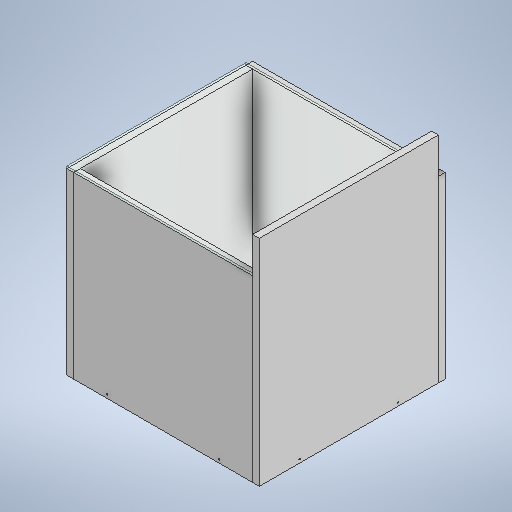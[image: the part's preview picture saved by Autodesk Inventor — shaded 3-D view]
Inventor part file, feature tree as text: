
AUTODESK INVENTOR PART (.ipt)
format: ipt  version: 2025.1 (Build 291241000, 241)  size: 359,936 bytes
history: native  units: mm
features: other x25, extrude x12, sketch x12, imported_body x1
ambient origin geometry x8: Origin, YZ Plane, XZ Plane, XY Plane, X Axis, Y Axis, Z Axis, Center Point
bodies: Body1 (feature_tree), Body2 (feature_tree), Body3 (feature_tree), Body4 (feature_tree), Body5 (feature_tree), Body6 (feature_tree), Body7 (feature_tree)
feature tree (50):
  other  "Sólido1"
  extrude  "Extrusão1"  Depth=400.0mm
  extrude  "Extrusão2"  Depth=200.0mm
  extrude  "Extrusão4"  Depth=400.0mm
  extrude  "Extrusão9"  Depth=15.0mm TaperAngle=0.0deg
  extrude  "Extrusão10"  Depth=400.0mm
  extrude  "Extrusão11"  Depth=15.0mm TaperAngle=0.0deg
  other  "Plano de trabalho1"
  extrude  "Extrusão12"  Depth=5.0mm
  extrude  "Extrusão13"  Depth=75.0mm
  extrude  "Extrusão14"  Depth=75.0mm
  extrude  "Extrusão15"  Depth=40.0mm
  extrude  "Extrusão16"  Depth=15.0mm TaperAngle=0.0deg
  extrude  "Extrusão17"  Depth=75.0mm
  sketch  "Esboço1"  dims[d0=400.0mm d1=400.0mm]
  sketch  "Esboço2"  dims[d2=200.0mm d3=200.0mm]
  other  "Contorno projetado1"
  other  "Sólido2"
  sketch  "Esboço4"  dims[d4=15.0mm d5=0.0mm d7=400.0mm]
  other  "Contorno projetado5"
  other  "Contorno projetado6"
  other  "Sólido4"
  imported_body  "base"
  sketch  "Esboço10"  dims[d8=15.0mm d9=0.0mm d12=15.0mm d13=0.0mm]
  other  "Contorno projetado17"
  other  "Contorno projetado18"
  other  "Sólido9"
  sketch  "Esboço11"  dims[d29=15.0mm d30=0.0mm d31=400.0mm]
  sketch  "Esboço12"  dims[d32=80.0mm d33=15.0mm d34=0.0mm]
  other  "Contorno projetado19"
  other  "vidro"
  sketch  "Esboço15"  dims[d35=5.0mm d36=0.0mm d37=3.0mm]
  sketch  "Esboço16"  dims[d38=75.0mm d39=3.0mm]
  other  "Contorno projetado23"
  other  "Contorno projetado24"
  other  "Contorno projetado25"
  other  "Sólido11"
  sketch  "Esboço17"  dims[d40=75.0mm d41=7.5mm]
  other  "Contorno projetado26"
  other  "Contorno projetado27"
  other  "Contorno projetado28"
  other  "Contorno projetado29"
  sketch  "Esboço18"  dims[d42=50000.0mm d43=0.0mm d44=40.0mm]
  other  "Contorno projetado30"
  other  "Contorno projetado31"
  other  "Contorno projetado32"
  other  "Sólido12"
  other  "Contorno projetado33"
  sketch  "Esboço19"  dims[d45=15.0mm d46=0.0mm d47=15.0mm d48=0.0mm]
  sketch  "Esboço20"  dims[d49=15.0mm d50=0.0mm d51=4.0mm d52=75.0mm d53=7.5mm d54=4.0mm d55=75.0mm d56=5000.0mm d57=0.0mm d58=4.0mm d59=75.0mm d60=20.0mm d61=4.0mm d62=75.0mm d63=20.0mm d64=5000.0mm d65=0.0mm d18=0.5mm d19=0.872665mm d20=0.5mm d21=0.872665mm]
